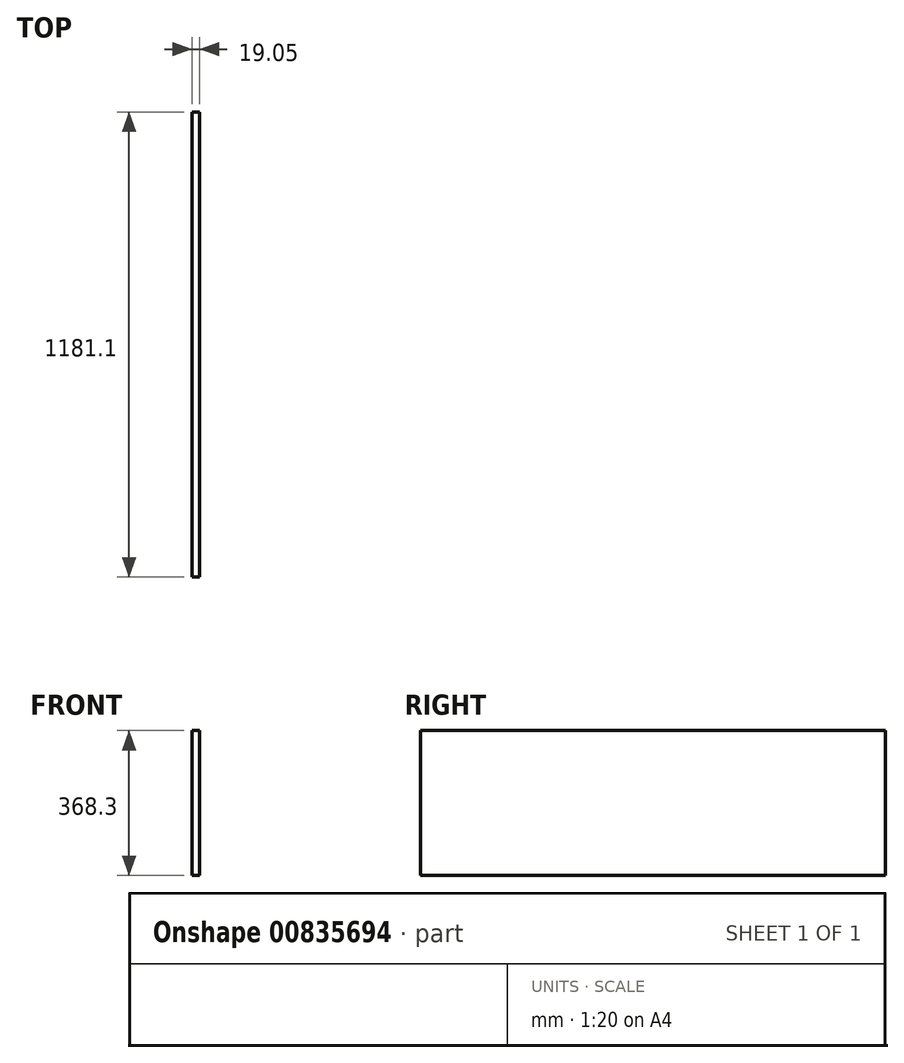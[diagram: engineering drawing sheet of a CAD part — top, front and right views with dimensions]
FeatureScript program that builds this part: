
annotation { "Feature Type Name" : "Feature", "Feature Type Description" : "" }
export const myFeature = defineFeature(function(context is Context, id is Id, definition is map)
    precondition{}
    {
        {
            var Q0;
            Q0=qCreatedBy(makeId("Right.planeOp"),FACE);
            var sketch = newSketch(context, id + "F0", { "sketchPlane" : qUnion([Q0])});
            skLineSegment(sketch, "E0.bottom", {"start": v(0, 0) * mm, "end": v(1181.1, 0) * mm});
            skLineSegment(sketch, "E0.top", {"start": v(0, 368.3) * mm, "end": v(1181.1, 368.3) * mm});
            skLineSegment(sketch, "E0.left", {"start": v(0, 0) * mm, "end": v(0, 368.3) * mm});
            skLineSegment(sketch, "E0.right", {"start": v(1181.1, 0) * mm, "end": v(1181.1, 368.3) * mm});
            skSolve(sketch);
        }
        {
            var Q0;
            Q0=qSketchRegion(id+"F0",true);
            extrude(context, id + "F1", {"entities" : qUnion([Q0]), "depth" : 19.05 * mm, "offsetDistance" : 25.4 * mm});
        }
    });
